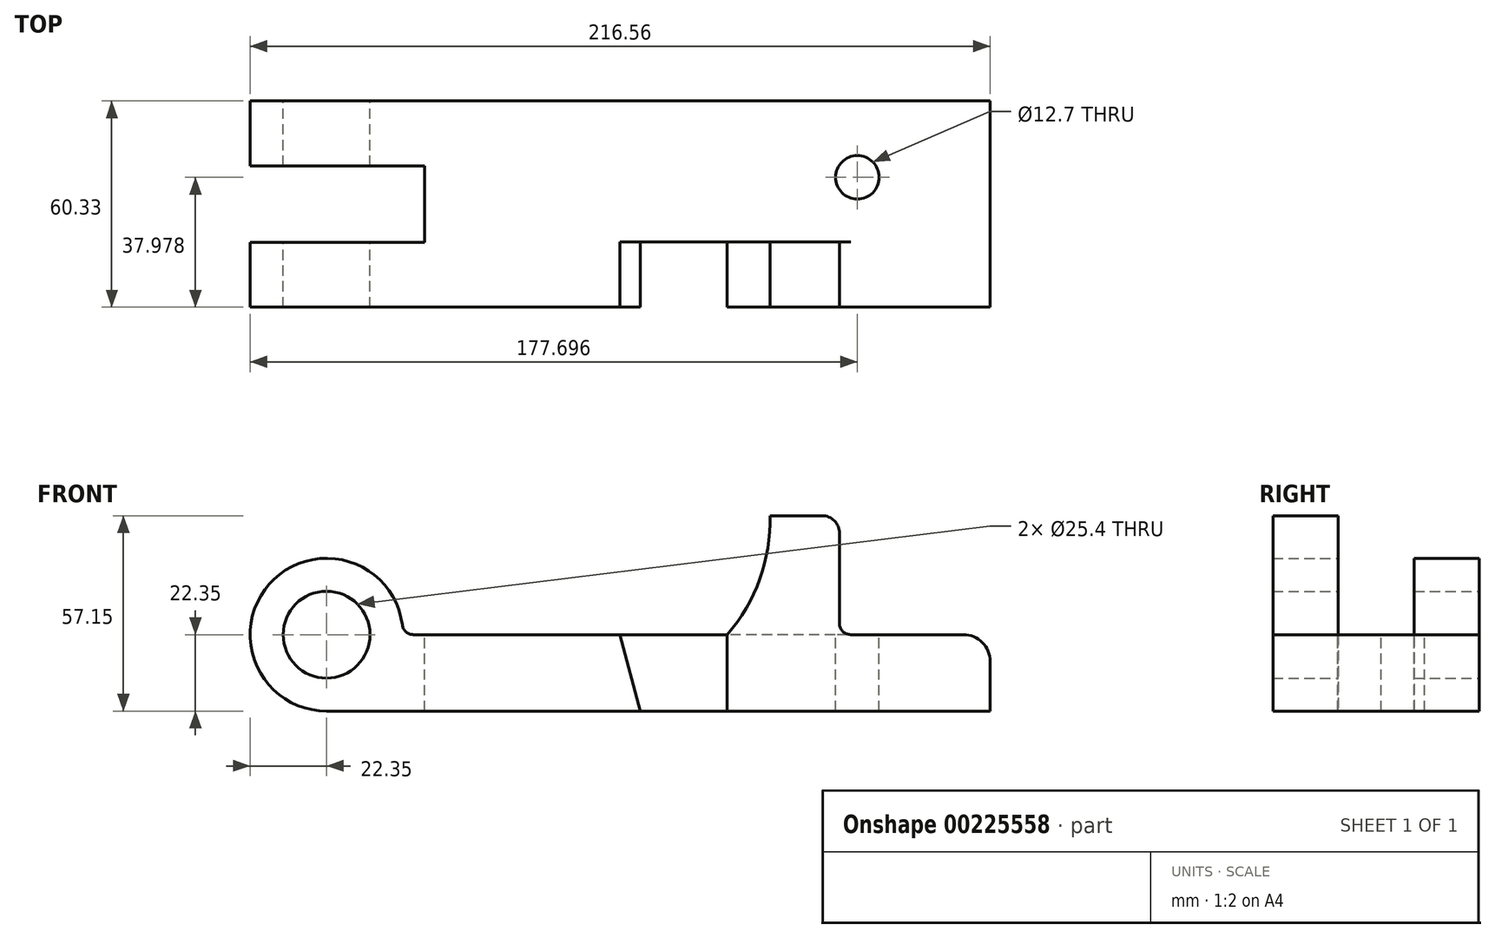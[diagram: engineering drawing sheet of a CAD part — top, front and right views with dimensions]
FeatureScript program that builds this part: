
annotation { "Feature Type Name" : "Feature", "Feature Type Description" : "" }
export const myFeature = defineFeature(function(context is Context, id is Id, definition is map)
    precondition{}
    {
        {
            var Q0;
            Q0=qCreatedBy(makeId("Front.planeOp"),FACE);
            var sketch = newSketch(context, id + "F0", { "sketchPlane" : qUnion([Q0])});
            skArc(sketch, "E0", {"start": v(22.35, 0) * mm, "mid": v(-15.8, 15.8) * mm, "end": v(0, -22.35) * mm});
            skCircle(sketch, "E1", {"center": v(0, 0) * mm, "radius": 12.7 * mm});
            skLineSegment(sketch, "E2", {"start": v(22.35, 0) * mm, "end": v(117.25, 0) * mm});
            skLineSegment(sketch, "E3", {"start": v(129.77, 34.8) * mm, "end": v(150.09, 34.8) * mm});
            skLineSegment(sketch, "E4", {"start": v(150.09, 34.8) * mm, "end": v(150.09, 0) * mm});
            skLineSegment(sketch, "E5", {"start": v(150.09, 0) * mm, "end": v(194.2, 0) * mm});
            skLineSegment(sketch, "E6", {"start": v(0, -22.35) * mm, "end": v(194.2, -22.35) * mm});
            skLineSegment(sketch, "E7", {"start": v(194.2, -22.35) * mm, "end": v(194.2, 0) * mm});
            skArc(sketch, "E8", {"start": v(117.25, 0) * mm, "mid": v(126.79, 16.22) * mm, "end": v(129.77, 34.8) * mm});
            skSolve(sketch);
        }
        {
            var Q0;
            Q0 = qSketchRegion(id + "F0", true);
            extrude(context, id + "F1", {"entities" : qUnion([Q0]), "depth" : 60.32 * mm});
        }
        {
            var Q0;
            Q0=makeQuery(id+"F1.opExtrude","SWEPT_EDGE",EDGE,{"disambiguationData":[OSD([sQuery(id+"F0.wireOp",EDGE,"E0"),sQuery(id+"F0.wireOp",EDGE,"E2")])]});
            var Q1;
            Q1=makeQuery(id+"F1.opExtrude","SWEPT_EDGE",EDGE,{"disambiguationData":[OSD([sQuery(id+"F0.wireOp",EDGE,"E4"),sQuery(id+"F0.wireOp",EDGE,"E5")])]});
            fillet(context, id + "F2", {"entities" : qUnion([Q0, Q1]), "radius" : 3.3 * mm, "tangentPropagation" : true, "allowEdgeOverflow" : false});
        }
        {
            var Q0;
            Q0=makeQuery(id+"F1.opExtrude","SWEPT_FACE",FACE,{"disambiguationData":[OSD([sQuery(id+"F0.wireOp",EDGE,"E3")])]});
            var sketch = newSketch(context, id + "F3", { "sketchPlane" : qUnion([Q0])});
            skLineSegment(sketch, "E9.bottom", {"start": v(-28.74, -19) * mm, "end": v(28.74, -19) * mm});
            skLineSegment(sketch, "E9.top", {"start": v(-28.74, -41.33) * mm, "end": v(28.74, -41.33) * mm});
            skLineSegment(sketch, "E9.left", {"start": v(-28.74, -19) * mm, "end": v(-28.74, -41.33) * mm});
            skLineSegment(sketch, "E9.right", {"start": v(28.74, -19) * mm, "end": v(28.74, -41.33) * mm});
            skPoint(sketch, "E9.middle", {"position": v(0, -30.16) * mm});
            skLineSegment(sketch, "E10.bottom", {"start": v(106.92, -41.28) * mm, "end": v(163.55, -41.28) * mm});
            skLineSegment(sketch, "E10.top", {"start": v(106.92, 0) * mm, "end": v(163.55, 0) * mm});
            skLineSegment(sketch, "E10.left", {"start": v(106.92, -41.28) * mm, "end": v(106.92, 0) * mm});
            skLineSegment(sketch, "E10.right", {"start": v(163.55, -41.28) * mm, "end": v(163.55, 0) * mm});
            skSolve(sketch);
        }
        {
            var Q0;
            Q0=makeQuery(id+"F3.imprint","IMPRINT",FACE,{"disambiguationData":[TD([[makeQuery(id+"F3.imprint","IMPRINT",EDGE,{"derivedFrom":sQuery(id+"F3.wireOp",EDGE,"E9.bottom")}),-1.0]])]});
            extrude(context, id + "F4", {"entities" : qUnion([Q0]), "operationType" : NewBodyOperationType.REMOVE, "endBound" : BoundingType.THROUGH_ALL, "oppositeDirection" : true, "depth" : 25.4 * mm});
        }
        {
            var Q0;
            {var subQ0=sQuery(id+"F3.wireOp",EDGE,"E10.left");Q0=makeQuery(id+"F3.imprint","IMPRINT",FACE,{"disambiguationData":[TD([[makeQuery(id+"F3.imprint","IMPRINT",EDGE,{"derivedFrom":subQ0}),-1.0]])]});}
            var Q1;
            {var subQ0=sQuery(id+"F3.wireOp",EDGE,"E10.bottom");var subQ1=sQuery(id+"F0.wireOp",EDGE,"E3");var subQ2=makeQuery(id+"F1.opExtrude","SWEPT_EDGE",EDGE,{"disambiguationData":[OSD([subQ1,sQuery(id+"F0.wireOp",EDGE,"E8")])]});var subQ3=makeQuery(id+"F3.imprint","INTERSECT",VERTEX,{"derivedFrom":[subQ2,subQ0]});Q1=makeQuery(id+"F3.imprint","IMPRINT",FACE,{"disambiguationData":[TD([[makeQuery(id+"F3.imprint","IMPRINT",EDGE,{"disambiguationData":[TD([[subQ3,-1.0]])],"derivedFrom":subQ0}),1.0]])]});}
            var Q2;
            {var subQ0=sQuery(id+"F3.wireOp",EDGE,"E10.right");Q2=makeQuery(id+"F3.imprint","IMPRINT",FACE,{"disambiguationData":[TD([[makeQuery(id+"F3.imprint","IMPRINT",EDGE,{"derivedFrom":subQ0}),1.0]])]});}
            var Q3;
            Q3=makeQuery(id+"F1.opExtrude","SWEPT_FACE",FACE,{"disambiguationData":[OSD([sQuery(id+"F0.wireOp",EDGE,"E5")])]});
            extrude(context, id + "F5", {"entities" : qUnion([Q0, Q1, Q2]), "operationType" : NewBodyOperationType.REMOVE, "endBound" : BoundingType.UP_TO_SURFACE, "oppositeDirection" : true, "endBoundEntityFace" : qUnion([Q3]), "depth" : 25.4 * mm});
        }
        {
            var Q0;
            {var subQ0=sQuery(id+"F0.wireOp",EDGE,"E5");Q0=makeQuery(id+"F5.boolean.opBoolean","MERGE",FACE,{"derivedFrom":[makeQuery(id+"F1.opExtrude","SWEPT_FACE",FACE,{"disambiguationData":[OSD([subQ0])]}),makeQuery(id+"F1.opExtrude","SWEPT_FACE",FACE,{"disambiguationData":[OSD([sQuery(id+"F0.wireOp",EDGE,"E2")])]}),makeQuery(id+"F5.opExtrude","CAP_FACE",FACE,{"disambiguationData":[OSD([subQ0])],"isStart":false})]});}
            var sketch = newSketch(context, id + "F6", { "sketchPlane" : qUnion([Q0])});
            skCircle(sketch, "E11", {"center": v(155.35, -22.35) * mm, "radius": 6.35 * mm});
            skSolve(sketch);
        }
        {
            var Q0;
            Q0 = qSketchRegion(id + "F6", true);
            extrude(context, id + "F7", {"entities" : qUnion([Q0]), "operationType" : NewBodyOperationType.REMOVE, "endBound" : BoundingType.THROUGH_ALL, "oppositeDirection" : true, "depth" : 25.4 * mm});
        }
        {
            var Q0;
            Q0=makeQuery(id+"F1.opExtrude","SWEPT_EDGE",EDGE,{"disambiguationData":[OSD([sQuery(id+"F0.wireOp",EDGE,"E3"),sQuery(id+"F0.wireOp",EDGE,"E4")])]});
            fillet(context, id + "F8", {"entities" : qUnion([Q0]), "radius" : 5.08 * mm, "tangentPropagation" : true, "allowEdgeOverflow" : false});
        }
        {
            var Q0;
            Q0=makeQuery(id+"F1.opExtrude","SWEPT_EDGE",EDGE,{"disambiguationData":[OSD([sQuery(id+"F0.wireOp",EDGE,"E5"),sQuery(id+"F0.wireOp",EDGE,"E7")])]});
            fillet(context, id + "F9", {"entities" : qUnion([Q0]), "radius" : 7.87 * mm, "tangentPropagation" : true, "allowEdgeOverflow" : false});
        }
        {
            var Q0;
            Q0=makeQuery(id+"F1.opExtrude","CAP_FACE",FACE,{"disambiguationData":[OSD([sQuery(id+"F0.wireOp",EDGE,"E0"),sQuery(id+"F0.wireOp",EDGE,"E1"),sQuery(id+"F0.wireOp",EDGE,"E2"),sQuery(id+"F0.wireOp",EDGE,"E3"),sQuery(id+"F0.wireOp",EDGE,"E4"),sQuery(id+"F0.wireOp",EDGE,"E5"),sQuery(id+"F0.wireOp",EDGE,"E6"),sQuery(id+"F0.wireOp",EDGE,"E7"),sQuery(id+"F0.wireOp",EDGE,"E8")])],"isStart":false});
            var sketch = newSketch(context, id + "F10", { "sketchPlane" : qUnion([Q0])});
            skLineSegment(sketch, "E12", {"start": v(117.25, 0) * mm, "end": v(117.25, -22.35) * mm});
            skLineSegment(sketch, "E13", {"start": v(117.25, -22.35) * mm, "end": v(91.85, -22.35) * mm});
            skLineSegment(sketch, "E14", {"start": v(91.85, -22.35) * mm, "end": v(85.85, 0) * mm});
            skLineSegment(sketch, "E15", {"start": v(85.85, 0) * mm, "end": v(117.25, 0) * mm});
            skSolve(sketch);
        }
        {
            var Q0;
            Q0 = qSketchRegion(id + "F10", true);
            extrude(context, id + "F11", {"entities" : qUnion([Q0]), "operationType" : NewBodyOperationType.REMOVE, "oppositeDirection" : true, "depth" : 19.05 * mm});
        }
    });
